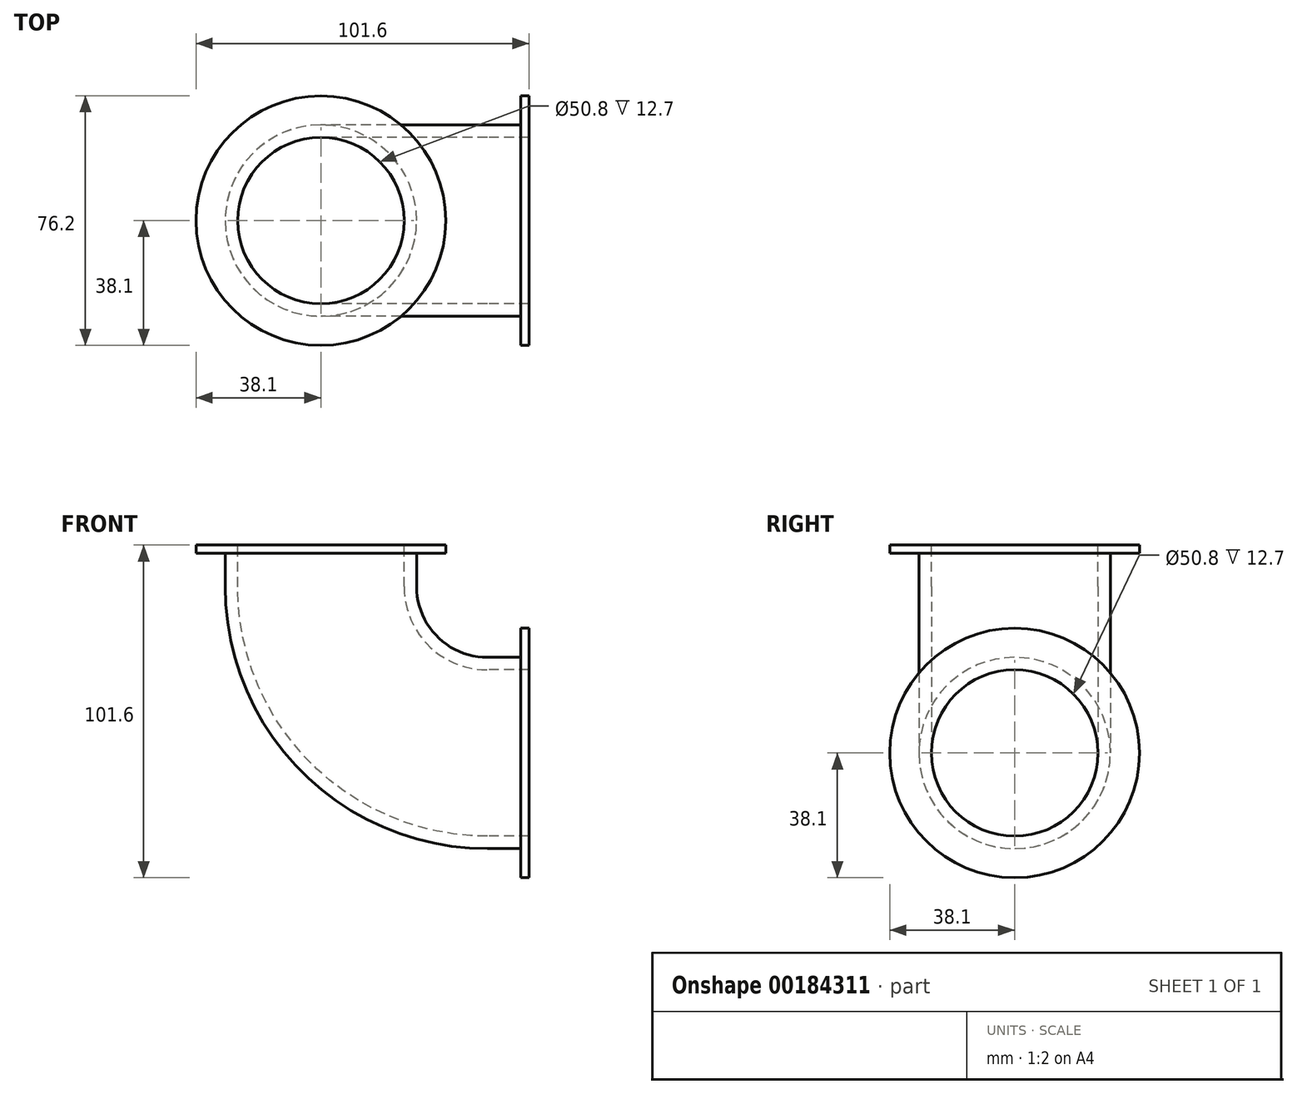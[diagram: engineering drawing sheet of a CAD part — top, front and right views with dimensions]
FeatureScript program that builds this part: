
annotation { "Feature Type Name" : "Feature", "Feature Type Description" : "" }
export const myFeature = defineFeature(function(context is Context, id is Id, definition is map)
    precondition{}
    {
        {
            var Q0;
            Q0=qCreatedBy(makeId("Front.planeOp"),FACE);
            var sketch = newSketch(context, id + "F0", { "sketchPlane" : qUnion([Q0])});
            skArc(sketch, "E0", {"start": v(-50.8, 50.8) * mm, "mid": v(-35.92, 14.88) * mm, "end": v(0, 0) * mm});
            skLineSegment(sketch, "E1", {"start": v(-50.8, 50.8) * mm, "end": v(-50.8, 63.5) * mm});
            skLineSegment(sketch, "E2", {"start": v(0, 0) * mm, "end": v(12.7, 0) * mm});
            skSolve(sketch);
        }
        {
            var Q0;
            Q0=qCreatedBy(makeId("Right.planeOp"),FACE);
            cPlane(context, id + "F1", {"entities" : qUnion([Q0]), "cplaneType" : CPlaneType.OFFSET, "offset" : 12.7 * mm, "width" : 152.4 * mm, "height" : 152.4 * mm});
        }
        {
            var Q0;
            Q0=qCreatedBy(id+"F1.planeOp",FACE);
            var sketch = newSketch(context, id + "F2", { "sketchPlane" : qUnion([Q0])});
            skCircle(sketch, "E3", {"center": v(0, 0) * mm, "radius": 25.4 * mm});
            skCircle(sketch, "E4", {"center": v(0, 0) * mm, "radius": 29.21 * mm});
            skSolve(sketch);
        }
        {
            var Q0;
            Q0=makeQuery(id+"F2.imprint","IMPRINT",FACE,{"disambiguationData":[TD([[makeQuery(id+"F2.imprint","IMPRINT",EDGE,{"derivedFrom":sQuery(id+"F2.wireOp",EDGE,"E3")}),-1.0]])]});
            var Q1;
            Q1=sQuery(id+"F0.wireOp",EDGE,"E2");
            var Q2;
            Q2=sQuery(id+"F0.wireOp",EDGE,"E0");
            var Q3;
            Q3=sQuery(id+"F0.wireOp",EDGE,"E1");
            sweep(context, id + "F3", {"profiles" : qUnion([Q0]), "path" : qUnion([Q1, Q2, Q3])});
        }
        {
            var Q0;
            Q0=makeQuery(id+"F3.opSweep","CAP_FACE",FACE,{"disambiguationData":[OSD([sQuery(id+"F0.wireOp",VERTEX,"E2.end"),sQuery(id+"F2.wireOp",EDGE,"E3"),sQuery(id+"F2.wireOp",EDGE,"E4")])],"isStart":true});
            var sketch = newSketch(context, id + "F4", { "sketchPlane" : qUnion([Q0])});
            skCircle(sketch, "E5", {"center": v(0, 0) * mm, "radius": 38.1 * mm});
            skCircle(sketch, "E6", {"center": v(0, 0) * mm, "radius": 25.4 * mm});
            skSolve(sketch);
        }
        {
            var Q0;
            Q0 = qSketchRegion(id + "F4", true);
            extrude(context, id + "F5", {"entities" : qUnion([Q0]), "operationType" : NewBodyOperationType.ADD, "oppositeDirection" : true, "depth" : 2.54 * mm});
        }
        {
            var Q0;
            Q0=makeQuery(id+"F3.opSweep","CAP_FACE",FACE,{"disambiguationData":[OSD([sQuery(id+"F0.wireOp",VERTEX,"E1.end"),sQuery(id+"F2.wireOp",EDGE,"E3"),sQuery(id+"F2.wireOp",EDGE,"E4")])],"isStart":false});
            var sketch = newSketch(context, id + "F6", { "sketchPlane" : qUnion([Q0])});
            skCircle(sketch, "E7", {"center": v(-50.8, 0) * mm, "radius": 25.4 * mm});
            skCircle(sketch, "E8", {"center": v(-50.8, 0) * mm, "radius": 38.1 * mm});
            skSolve(sketch);
        }
        {
            var Q0;
            Q0 = qSketchRegion(id + "F6", true);
            extrude(context, id + "F7", {"entities" : qUnion([Q0]), "operationType" : NewBodyOperationType.ADD, "oppositeDirection" : true, "depth" : 2.54 * mm});
        }
    });
